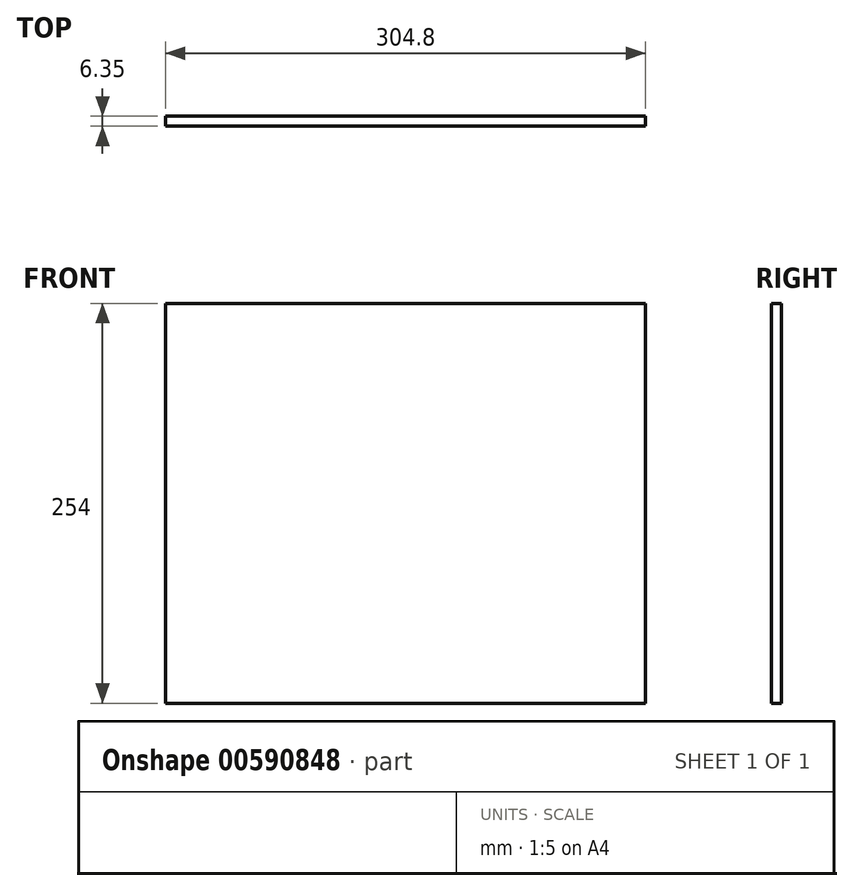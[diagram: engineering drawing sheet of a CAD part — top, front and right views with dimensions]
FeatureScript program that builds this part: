
annotation { "Feature Type Name" : "Feature", "Feature Type Description" : "" }
export const myFeature = defineFeature(function(context is Context, id is Id, definition is map)
    precondition{}
    {
        {
            var Q0;
            Q0=qCreatedBy(makeId("Front.planeOp"),FACE);
            var sketch = newSketch(context, id + "F0", { "sketchPlane" : qUnion([Q0])});
            skLineSegment(sketch, "E0", {"start": v(-116.99, 138.78) * mm, "end": v(-116.99, -115.22) * mm});
            skLineSegment(sketch, "E1", {"start": v(-116.99, -115.22) * mm, "end": v(187.81, -115.22) * mm});
            skLineSegment(sketch, "E2", {"start": v(187.81, -115.22) * mm, "end": v(187.81, 138.78) * mm});
            skLineSegment(sketch, "E3", {"start": v(187.81, 138.78) * mm, "end": v(-116.99, 138.78) * mm});
            skSolve(sketch);
        }
        {
            var Q0;
            Q0=makeQuery(id+"F0.imprint","IMPRINT",FACE,{"disambiguationData":[TD([[makeQuery(id+"F0.imprint","IMPRINT",EDGE,{"derivedFrom":sQuery(id+"F0.wireOp",EDGE,"E0")}),1.0]])]});
            extrude(context, id + "F1", {"entities" : qUnion([Q0]), "depth" : 6.35 * mm, "offsetDistance" : 25.4 * mm});
        }
    });
